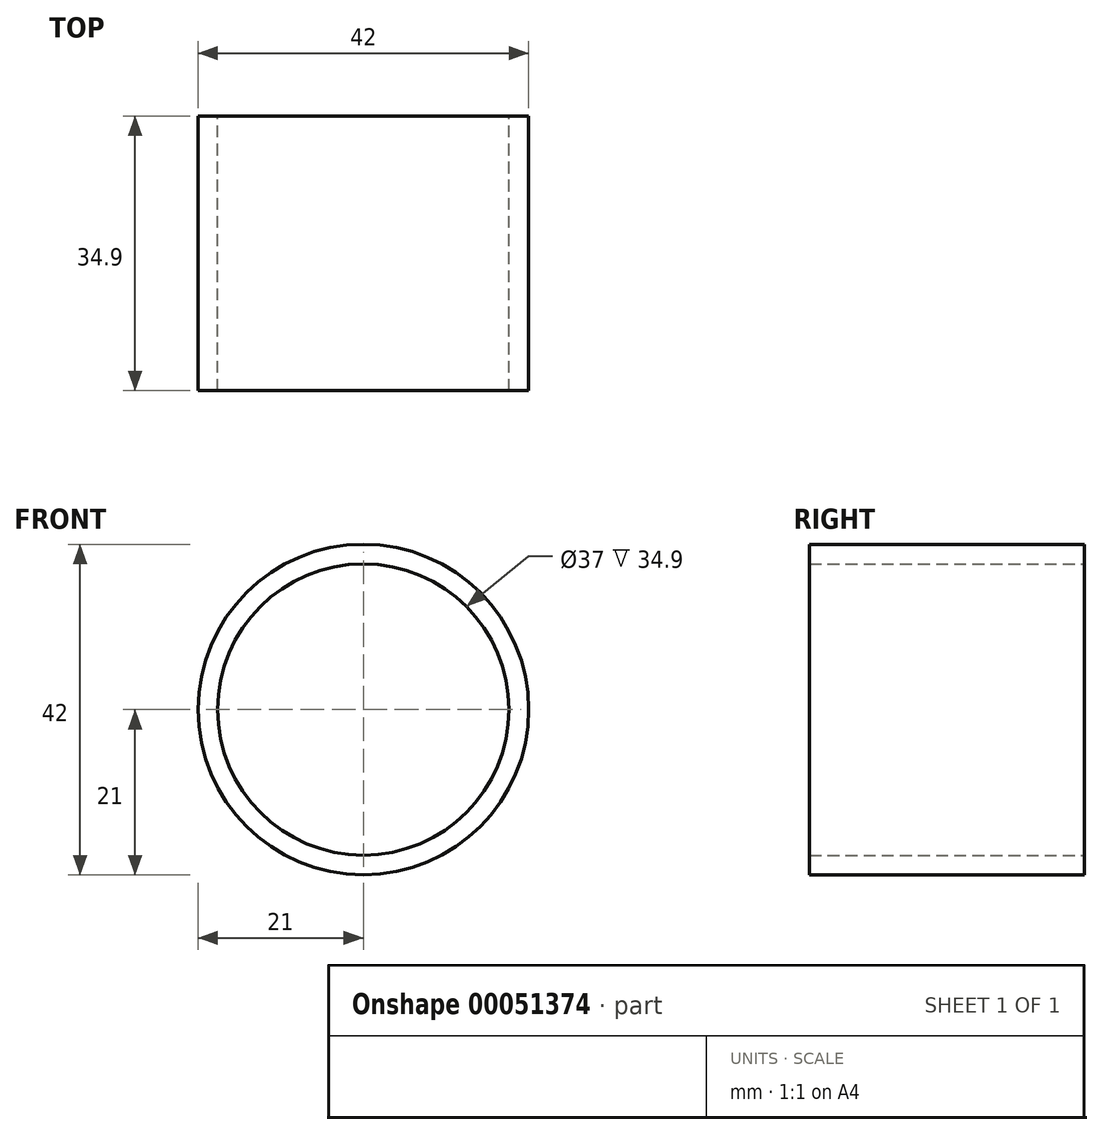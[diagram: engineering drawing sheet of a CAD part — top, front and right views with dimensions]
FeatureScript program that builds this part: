
annotation { "Feature Type Name" : "Feature", "Feature Type Description" : "" }
export const myFeature = defineFeature(function(context is Context, id is Id, definition is map)
    precondition{}
    {
        {
            var Q0;
            Q0=qCreatedBy(makeId("Front.planeOp"),FACE);
            var sketch = newSketch(context, id + "F0", { "sketchPlane" : qUnion([Q0])});
            skCircle(sketch, "E0", {"center": v(0, 0) * mm, "radius": 21 * mm});
            skCircle(sketch, "E1", {"center": v(0, 0) * mm, "radius": 18.5 * mm});
            skSolve(sketch);
        }
        {
            var Q0;
            Q0=qSketchRegion(id+"F0",true);
            extrude(context, id + "F1", {"entities" : qUnion([Q0]), "depth" : 17.45 * mm, "hasSecondDirection" : true, "secondDirectionOppositeDirection" : true, "secondDirectionDepth" : 17.45 * mm});
        }
    });
